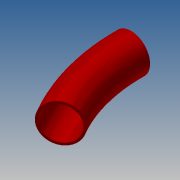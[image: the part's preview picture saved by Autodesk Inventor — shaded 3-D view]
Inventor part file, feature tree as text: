
AUTODESK INVENTOR PART (.ipt)
format: ipt  version: 2017.3 (Build 213257000, 257)  size: 151,040 bytes
history: native  units: in
note: dims shown in document units (in); Inventor stores cm internally (conversion verified against a paired STEP export)
features: other x3, revolve x1, sketch x1
ambient origin geometry x8: Origin, YZ Plane, XZ Plane, XY Plane, X Axis, Y Axis, Z Axis, Center Point
bodies: Solid1 (feature_tree)
feature tree (5):
  other  "A1-19027-100-08 HCWI elbow - center.ipt"
  revolve  "Revolution1"  [1 undecoded]
  other  "Solid1::A1-19027-100-08 HCWI elbow - center.ipt"
  other  "TaggingFeature1"
  sketch  "Sketch1"  dims[d0=0.3937in d1=2.0in d2=0.2096in d3=0.0034in]
note: 1 required parameter value undecoded (feature->parameter linkage not recoverable at this tier; creation-order binding heuristic only, values carry confidence <= 0.55)
